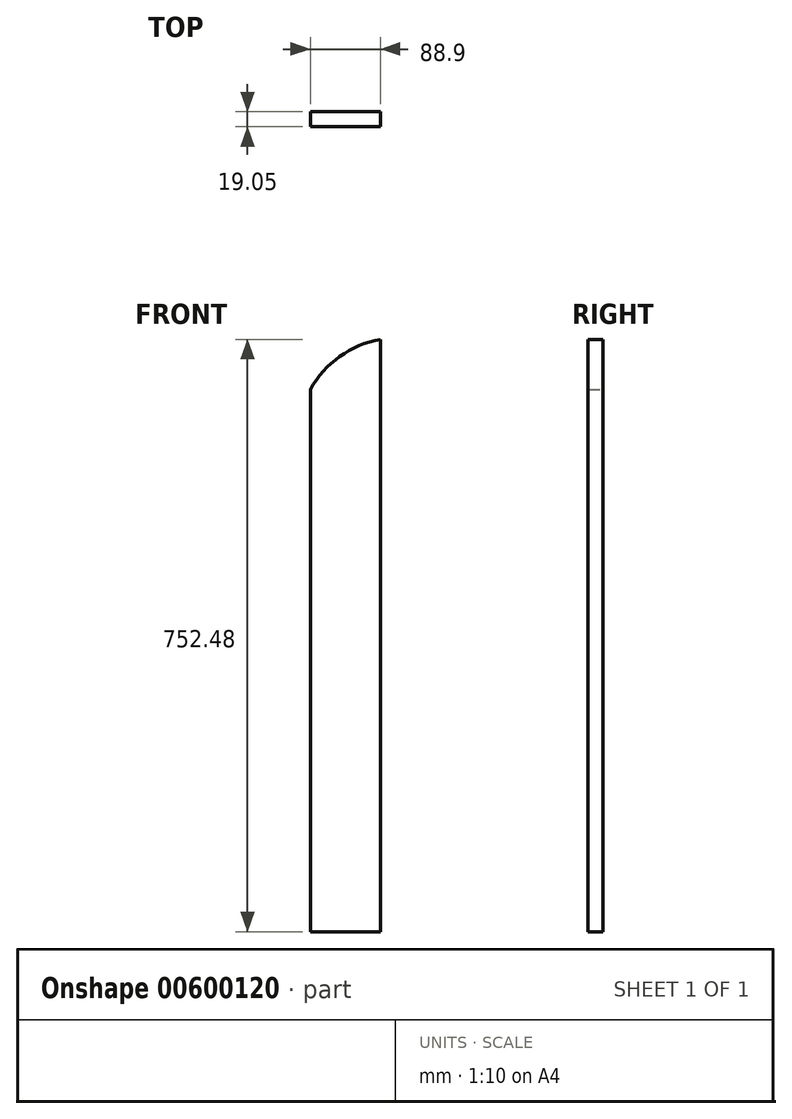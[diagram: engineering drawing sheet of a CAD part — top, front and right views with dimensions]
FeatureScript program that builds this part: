
annotation { "Feature Type Name" : "Feature", "Feature Type Description" : "" }
export const myFeature = defineFeature(function(context is Context, id is Id, definition is map)
    precondition{}
    {
        {
            var Q0;
            Q0=qCreatedBy(makeId("Front.planeOp"),FACE);
            var sketch = newSketch(context, id + "F0", { "sketchPlane" : qUnion([Q0])});
            skLineSegment(sketch, "E0.bottom", {"start": v(0, 0) * mm, "end": v(-88.9, 0) * mm});
            skLineSegment(sketch, "E0.top", {"start": v(0, 752.48) * mm, "end": v(-88.9, 752.48) * mm, "construction": true});
            skLineSegment(sketch, "E0.left", {"start": v(0, 0) * mm, "end": v(0, 752.48) * mm});
            skLineSegment(sketch, "E0.right", {"start": v(-88.9, 0) * mm, "end": v(-88.9, 752.48) * mm, "construction": true});
            skLineSegment(sketch, "E1", {"start": v(-88.9, 0) * mm, "end": v(-88.9, 688.98) * mm});
            skArc(sketch, "E2", {"start": v(0, 752.48) * mm, "mid": v(-51.63, 730.77) * mm, "end": v(-88.9, 688.98) * mm});
            skSolve(sketch);
        }
        {
            var Q0;
            Q0 = qSketchRegion(id + "F0", true);
            extrude(context, id + "F1", {"entities" : qUnion([Q0]), "depth" : 19.05 * mm, "offsetDistance" : 25.4 * mm});
        }
    });
